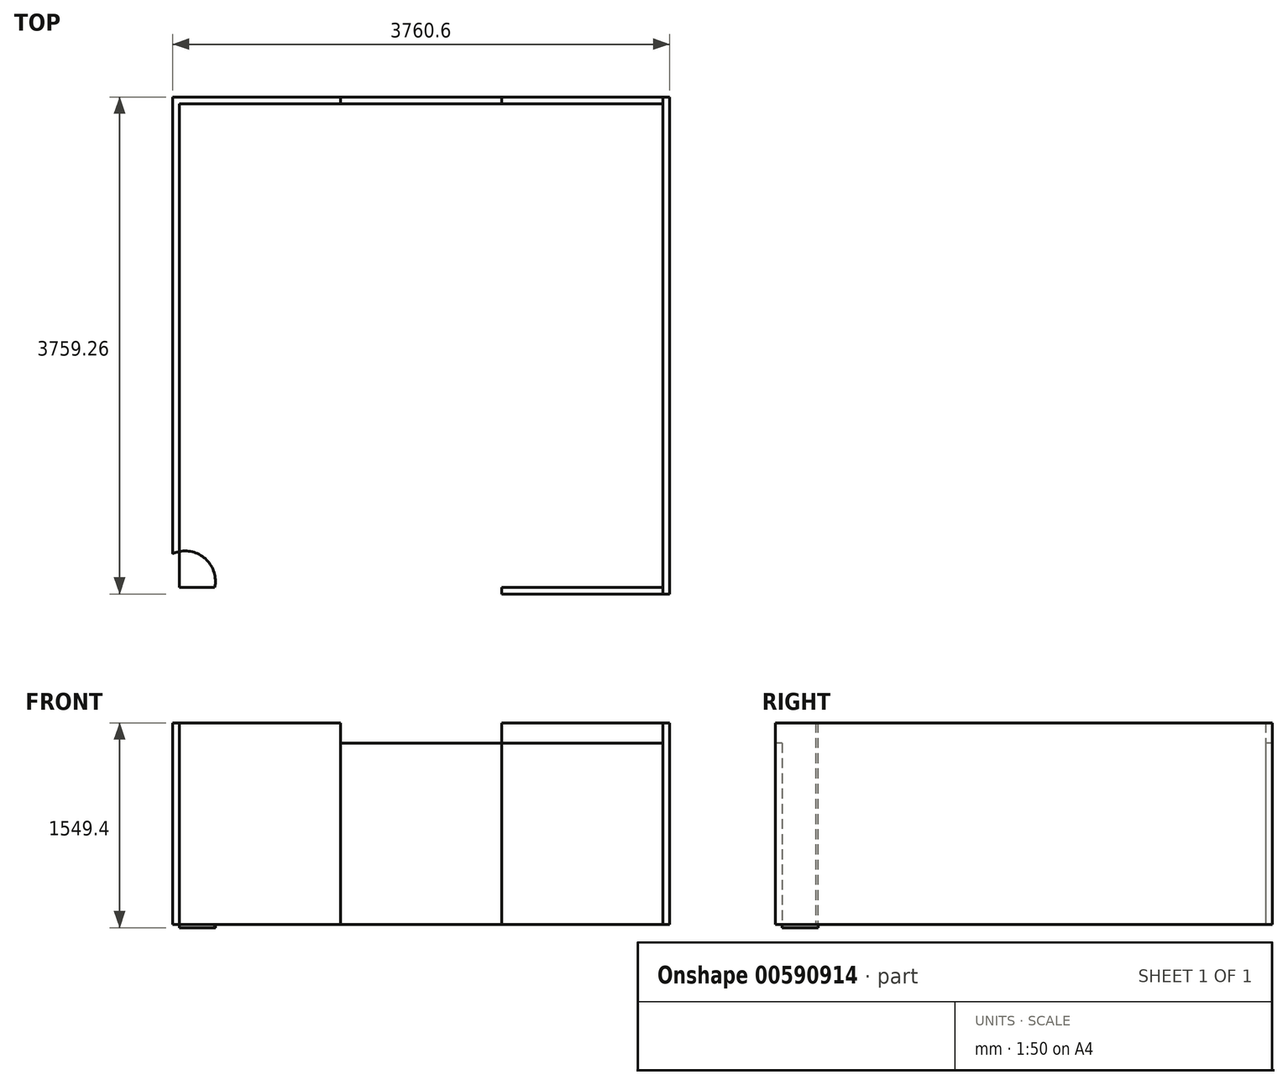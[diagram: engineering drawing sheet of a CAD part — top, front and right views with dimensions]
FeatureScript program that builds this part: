
annotation { "Feature Type Name" : "Feature", "Feature Type Description" : "" }
export const myFeature = defineFeature(function(context is Context, id is Id, definition is map)
    precondition{}
    {
        {
            var Q0;
            Q0=qCreatedBy(makeId("Top.planeOp"),FACE);
            var sketch = newSketch(context, id + "F0", { "sketchPlane" : qUnion([Q0])});
            skLineSegment(sketch, "E0.bottom", {"start": v(0, 0) * mm, "end": v(3657.6, 0) * mm});
            skLineSegment(sketch, "E0.top", {"start": v(0, 3657.6) * mm, "end": v(3657.6, 3657.6) * mm});
            skLineSegment(sketch, "E0.left", {"start": v(0, 0) * mm, "end": v(0, 3657.6) * mm});
            skLineSegment(sketch, "E0.right", {"start": v(3657.6, 0) * mm, "end": v(3657.6, 3657.6) * mm});
            skLineSegment(sketch, "E1", {"start": v(3657.6, 0.02) * mm, "end": v(2438.34, 0.02) * mm});
            skLineSegment(sketch, "E2", {"start": v(2438.34, 0.02) * mm, "end": v(2438.34, -50.78) * mm});
            skLineSegment(sketch, "E3", {"start": v(2438.34, -50.78) * mm, "end": v(3657.54, -50.78) * mm});
            skLineSegment(sketch, "E4", {"start": v(3657.54, -50.78) * mm, "end": v(3657.6, 0.02) * mm});
            skLineSegment(sketch, "E5", {"start": v(2438.34, -50.78) * mm, "end": v(0, -50.78) * mm});
            skLineSegment(sketch, "E6", {"start": v(0, -50.78) * mm, "end": v(-52.26, -50.78) * mm});
            skLineSegment(sketch, "E7", {"start": v(-52.26, -50.78) * mm, "end": v(-52.26, 3708.42) * mm});
            skPoint(sketch, "E8.start.orphan", {"position": v(0, 3707.47) * mm});
            skLineSegment(sketch, "E9", {"start": v(-52.26, 3708.42) * mm, "end": v(3706.94, 3708.42) * mm});
            skPoint(sketch, "E10.start.orphan", {"position": v(3831.22, 3657.6) * mm});
            skPoint(sketch, "E11.start.orphan", {"position": v(3831.22, 0) * mm});
            skLineSegment(sketch, "E12", {"start": v(3657.54, -50.78) * mm, "end": v(3708.34, -50.84) * mm});
            skLineSegment(sketch, "E13", {"start": v(3706.94, 3708.42) * mm, "end": v(3708.34, -50.84) * mm});
            skLineSegment(sketch, "E14", {"start": v(1219.2, 3708.42) * mm, "end": v(1219.2, 3657.6) * mm});
            skLineSegment(sketch, "E15", {"start": v(1219.2, 3657.6) * mm, "end": v(2438.4, 3657.6) * mm});
            skLineSegment(sketch, "E16", {"start": v(2438.4, 3657.6) * mm, "end": v(2438.4, 3708.42) * mm});
            skLineSegment(sketch, "E17", {"start": v(0, 3707.47) * mm, "end": v(0, 3657.6) * mm});
            skLineSegment(sketch, "E18", {"start": v(3657.6, 3708.42) * mm, "end": v(3657.6, 3657.6) * mm});
            skCircle(sketch, "E19", {"center": v(43.7, 45.31) * mm, "radius": 228.6 * mm});
            skSolve(sketch);
        }
        {
            var Q0;
            {var subQ5=sQuery(id+"F0.wireOp",EDGE,"E3");Q0=makeQuery(id+"F0.imprint","IMPRINT",FACE,{"disambiguationData":[TD([[makeQuery(id+"F0.imprint","IMPRINT",EDGE,{"derivedFrom":subQ5}),1.0]])]});}
            extrude(context, id + "F1", {"entities" : qUnion([Q0]), "depth" : 1371.6 * mm, "offsetDistance" : 25.4 * mm});
        }
        {
            var Q0;
            {var subQ0=sQuery(id+"F0.wireOp",EDGE,"E14");Q0=makeQuery(id+"F0.imprint","IMPRINT",FACE,{"disambiguationData":[TD([[makeQuery(id+"F0.imprint","IMPRINT",EDGE,{"derivedFrom":subQ0}),1.0]])]});}
            extrude(context, id + "F2", {"entities" : qUnion([Q0]), "depth" : 1371.6 * mm, "offsetDistance" : 25.4 * mm});
        }
        {
            var Q0;
            {var subQ2=sQuery(id+"F0.wireOp",EDGE,"E16");Q0=makeQuery(id+"F0.imprint","IMPRINT",FACE,{"disambiguationData":[TD([[makeQuery(id+"F0.imprint","IMPRINT",EDGE,{"derivedFrom":subQ2}),-1.0]])]});}
            extrude(context, id + "F3", {"entities" : qUnion([Q0]), "operationType" : NewBodyOperationType.ADD, "depth" : 1524 * mm, "offsetDistance" : 25.4 * mm});
        }
        {
            var Q0;
            {var subQ4=sQuery(id+"F0.wireOp",EDGE,"E0.left");Q0=makeQuery(id+"F0.imprint","IMPRINT",FACE,{"disambiguationData":[TD([[makeQuery(id+"F0.imprint","IMPRINT",EDGE,{"derivedFrom":subQ4}),1.0]])]});}
            extrude(context, id + "F4", {"entities" : qUnion([Q0]), "depth" : 1524 * mm, "offsetDistance" : 25.4 * mm});
        }
        {
            var Q0;
            {var subQ5=sQuery(id+"F0.wireOp",EDGE,"E0.right");Q0=makeQuery(id+"F0.imprint","IMPRINT",FACE,{"disambiguationData":[TD([[makeQuery(id+"F0.imprint","IMPRINT",EDGE,{"derivedFrom":subQ5}),-1.0]])]});}
            extrude(context, id + "F5", {"entities" : qUnion([Q0]), "depth" : 1524 * mm, "offsetDistance" : 25.4 * mm});
        }
        {
            var Q0;
            {var subQ0=sQuery(id+"F0.wireOp",EDGE,"E0.left");Q0=makeQuery(id+"F0.imprint","IMPRINT",FACE,{"disambiguationData":[TD([[makeQuery(id+"F0.imprint","IMPRINT",EDGE,{"derivedFrom":subQ0}),-1.0]])]});}
            extrude(context, id + "F6", {"entities" : qUnion([Q0]), "oppositeDirection" : true, "depth" : 25.4 * mm, "offsetDistance" : 25.4 * mm});
        }
    });
